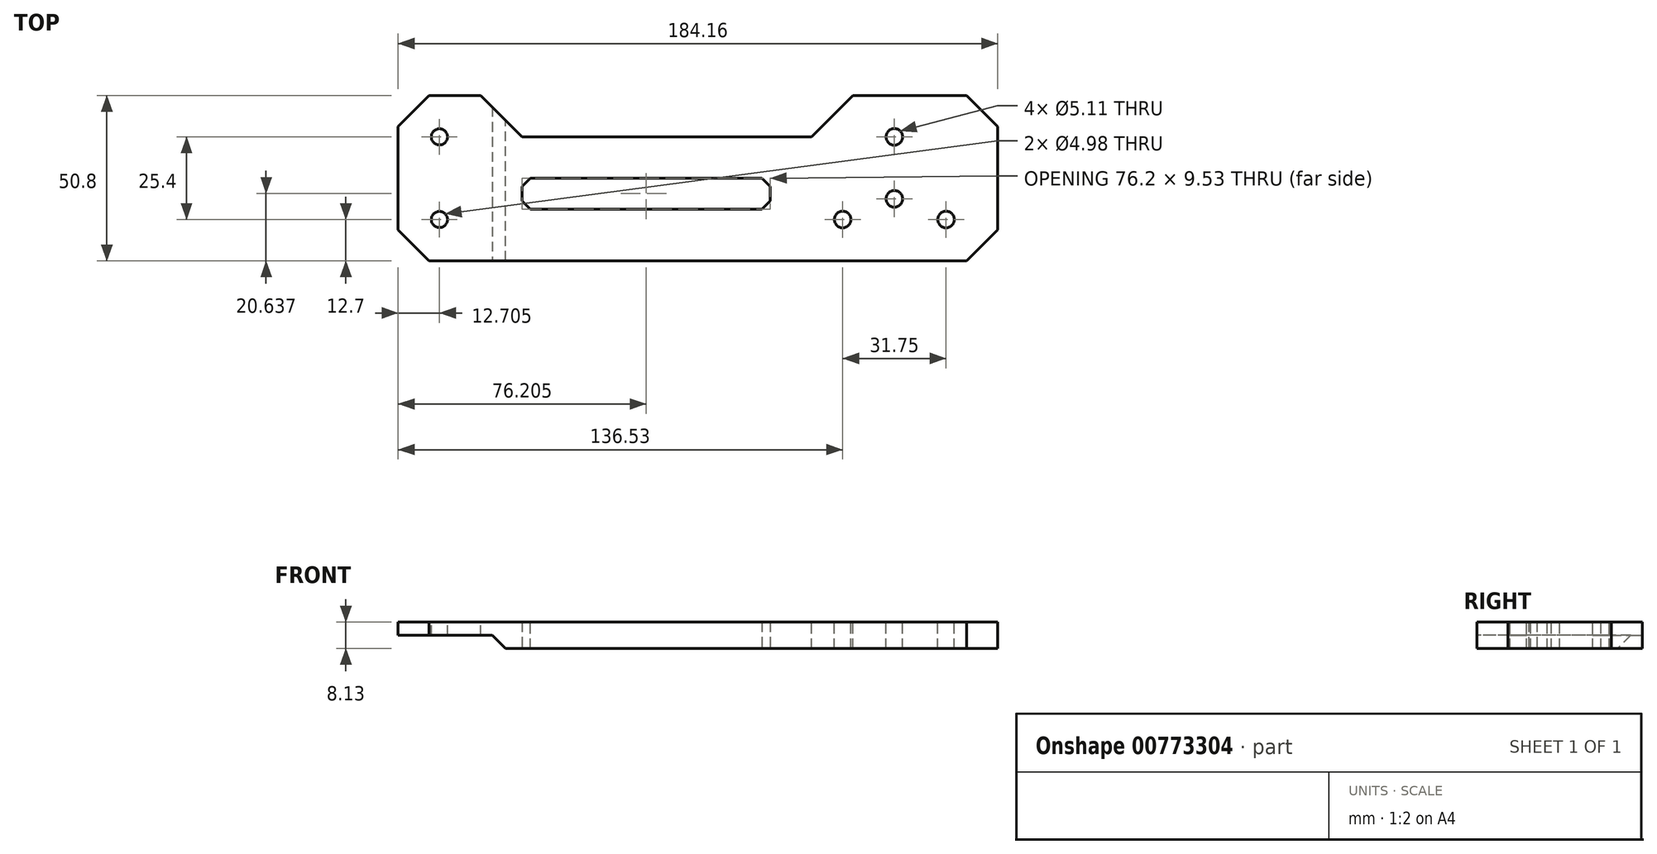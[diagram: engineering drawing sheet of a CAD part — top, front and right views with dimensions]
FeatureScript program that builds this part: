
annotation { "Feature Type Name" : "Feature", "Feature Type Description" : "" }
export const myFeature = defineFeature(function(context is Context, id is Id, definition is map)
    precondition{}
    {
        {
            var Q0;
            Q0=qCreatedBy(makeId("Top.planeOp"),FACE);
            var sketch = newSketch(context, id + "F0", { "sketchPlane" : qUnion([Q0])});
            skLineSegment(sketch, "E0.bottom", {"start": v(-92.08, 25.4) * mm, "end": v(92.08, 25.4) * mm});
            skLineSegment(sketch, "E0.top", {"start": v(-92.08, -25.4) * mm, "end": v(92.08, -25.4) * mm});
            skLineSegment(sketch, "E0.left", {"start": v(-92.08, 25.4) * mm, "end": v(-92.08, -25.4) * mm});
            skLineSegment(sketch, "E0.right", {"start": v(92.08, 25.4) * mm, "end": v(92.08, -25.4) * mm});
            skPoint(sketch, "E0.middle", {"position": v(0, 0) * mm});
            skSolve(sketch);
        }
        {
            var Q0;
            Q0=makeQuery(id+"F0.imprint","IMPRINT",FACE,{"disambiguationData":[TD([[makeQuery(id+"F0.imprint","IMPRINT",EDGE,{"derivedFrom":sQuery(id+"F0.wireOp",EDGE,"E0.bottom")}),-1.0]])]});
            extrude(context, id + "F1", {"entities" : qUnion([Q0]), "depth" : 8.13 * mm, "offsetDistance" : 25.4 * mm});
        }
        {
            var Q0;
            Q0=makeQuery(id+"F1.opExtrude","CAP_FACE",FACE,{"disambiguationData":[OSD([sQuery(id+"F0.wireOp",EDGE,"E0.bottom"),sQuery(id+"F0.wireOp",EDGE,"E0.top"),sQuery(id+"F0.wireOp",EDGE,"E0.left"),sQuery(id+"F0.wireOp",EDGE,"E0.right")])],"isStart":false});
            var sketch = newSketch(context, id + "F2", { "sketchPlane" : qUnion([Q0])});
            skPoint(sketch, "E1", {"position": v(-76.2, -12.7) * mm});
            skPoint(sketch, "E2", {"position": v(-44.45, -12.7) * mm});
            skPoint(sketch, "E3", {"position": v(-60.33, 12.7) * mm});
            skSolve(sketch);
        }
        {
            var Q0;
            Q0=sQuery(id+"F2.wireOp",VERTEX,"E3");
            var Q1;
            Q1=sQuery(id+"F2.wireOp",VERTEX,"E1");
            var Q2;
            Q2=sQuery(id+"F2.wireOp",VERTEX,"E2");
            var Q3;
            Q3=makeQuery(id+"F1.opExtrude","SWEPT_BODY",BODY,{"disambiguationData":[OSD([sQuery(id+"F0.wireOp",EDGE,"E0.bottom"),sQuery(id+"F0.wireOp",EDGE,"E0.top"),sQuery(id+"F0.wireOp",EDGE,"E0.left"),sQuery(id+"F0.wireOp",EDGE,"E0.right")])]});
            hole(context, id + "F3", {"style" : HoleStyle.SIMPLE, "endStyle" : HoleEndStyle.THROUGH, "standardTappedOrClearance" : lookupTablePath({ "standard" : "ANSI", "fit" : "Normal (ASME)", "size" : "#10", "type" : "Clearance" }), "standardBlindInLast" : lookupTablePath({ "fit" : "Free", "standard" : "ANSI", "size" : "#10", "type" : "Clearance" }), "holeDiameter" : 5.1 * mm, "majorDiameter" : 6.35 * mm, "isTappedThrough" : true, "tappedDepth" : 12.7 * mm, "tapClearance" : 3, "locations" : qUnion([Q0, Q1, Q2]), "scope" : qUnion([Q3])});
        }
        {
            var Q0;
            Q0=qCreatedBy(makeId("Right.planeOp"),FACE);
            cPlane(context, id + "F4", {"entities" : qUnion([Q0]), "cplaneType" : CPlaneType.OFFSET, "offset" : 60.32 * mm, "oppositeDirection" : true, "width" : 152.4 * mm, "height" : 152.4 * mm});
        }
        {
            var Q0;
            Q0=makeQuery(id+"F1.opExtrude","CAP_FACE",FACE,{"disambiguationData":[OSD([sQuery(id+"F0.wireOp",EDGE,"E0.bottom"),sQuery(id+"F0.wireOp",EDGE,"E0.top"),sQuery(id+"F0.wireOp",EDGE,"E0.left"),sQuery(id+"F0.wireOp",EDGE,"E0.right")])],"isStart":false});
            var sketch = newSketch(context, id + "F5", { "sketchPlane" : qUnion([Q0])});
            skPoint(sketch, "E4", {"position": v(79.38, 12.7) * mm});
            skPoint(sketch, "E5", {"position": v(79.38, -12.7) * mm});
            skSolve(sketch);
        }
        {
            var Q0;
            Q0=sQuery(id+"F5.wireOp",VERTEX,"E4");
            var Q1;
            Q1=sQuery(id+"F5.wireOp",VERTEX,"E5");
            var Q2;
            Q2=makeQuery(id+"F1.opExtrude","SWEPT_BODY",BODY,{"disambiguationData":[OSD([sQuery(id+"F0.wireOp",EDGE,"E0.bottom"),sQuery(id+"F0.wireOp",EDGE,"E0.top"),sQuery(id+"F0.wireOp",EDGE,"E0.left"),sQuery(id+"F0.wireOp",EDGE,"E0.right")])]});
            hole(context, id + "F6", {"style" : HoleStyle.SIMPLE, "endStyle" : HoleEndStyle.THROUGH, "standardTappedOrClearance" : lookupTablePath({ "standard" : "ANSI", "fit" : "Close", "size" : "#10", "type" : "Clearance" }), "standardBlindInLast" : lookupTablePath({ "fit" : "Close", "standard" : "ANSI", "size" : "#10", "type" : "Clearance" }), "holeDiameter" : 4.98 * mm, "majorDiameter" : 6.35 * mm, "isTappedThrough" : true, "tappedDepth" : 12.7 * mm, "tapClearance" : 3, "locations" : qUnion([Q0, Q1]), "scope" : qUnion([Q2])});
        }
        {
            var Q0;
            Q0=makeQuery(id+"F1.opExtrude","CAP_FACE",FACE,{"disambiguationData":[OSD([sQuery(id+"F0.wireOp",EDGE,"E0.bottom"),sQuery(id+"F0.wireOp",EDGE,"E0.top"),sQuery(id+"F0.wireOp",EDGE,"E0.left"),sQuery(id+"F0.wireOp",EDGE,"E0.right")])],"isStart":false});
            var sketch = newSketch(context, id + "F7", { "sketchPlane" : qUnion([Q0])});
            skLineSegment(sketch, "E6", {"start": v(-47.63, 25.4) * mm, "end": v(-34.92, 12.7) * mm});
            skLineSegment(sketch, "E7", {"start": v(-34.92, 12.7) * mm, "end": v(53.98, 12.7) * mm});
            skLineSegment(sketch, "E8", {"start": v(53.98, 12.7) * mm, "end": v(66.67, 25.4) * mm});
            skLineSegment(sketch, "E9", {"start": v(66.67, 25.4) * mm, "end": v(-47.63, 25.4) * mm});
            skLineSegment(sketch, "E10.bottom", {"start": v(-22.23, 0) * mm, "end": v(53.98, 0) * mm});
            skLineSegment(sketch, "E10.top", {"start": v(-22.23, -9.53) * mm, "end": v(53.98, -9.53) * mm});
            skLineSegment(sketch, "E10.left", {"start": v(-22.23, 0) * mm, "end": v(-22.23, -9.53) * mm});
            skLineSegment(sketch, "E10.right", {"start": v(53.98, 0) * mm, "end": v(53.98, -9.53) * mm});
            skPoint(sketch, "E10.middle", {"position": v(15.88, -4.76) * mm});
            skSolve(sketch);
        }
        {
            var Q0;
            Q0=makeQuery(id+"F7.imprint","IMPRINT",FACE,{"disambiguationData":[TD([[makeQuery(id+"F7.imprint","IMPRINT",EDGE,{"derivedFrom":sQuery(id+"F7.wireOp",EDGE,"E6")}),1.0]])]});
            var Q1;
            Q1=makeQuery(id+"F7.imprint","IMPRINT",FACE,{"disambiguationData":[TD([[makeQuery(id+"F7.imprint","IMPRINT",EDGE,{"derivedFrom":sQuery(id+"F7.wireOp",EDGE,"E10.bottom")}),-1.0]])]});
            extrude(context, id + "F8", {"entities" : qUnion([Q0, Q1]), "operationType" : NewBodyOperationType.REMOVE, "endBound" : BoundingType.THROUGH_ALL, "oppositeDirection" : true, "depth" : 25.4 * mm, "offsetDistance" : 25.4 * mm});
        }
        {
            var Q0;
            Q0=makeQuery(id+"F1.opExtrude","SWEPT_EDGE",EDGE,{"disambiguationData":[OSD([sQuery(id+"F0.wireOp",EDGE,"E0.top"),sQuery(id+"F0.wireOp",EDGE,"E0.left")])]});
            var Q1;
            Q1=makeQuery(id+"F1.opExtrude","SWEPT_EDGE",EDGE,{"disambiguationData":[OSD([sQuery(id+"F0.wireOp",EDGE,"E0.bottom"),sQuery(id+"F0.wireOp",EDGE,"E0.left")])]});
            var Q2;
            Q2=makeQuery(id+"F1.opExtrude","SWEPT_EDGE",EDGE,{"disambiguationData":[OSD([sQuery(id+"F0.wireOp",EDGE,"E0.top"),sQuery(id+"F0.wireOp",EDGE,"E0.right")])]});
            var Q3;
            Q3=makeQuery(id+"F1.opExtrude","SWEPT_EDGE",EDGE,{"disambiguationData":[OSD([sQuery(id+"F0.wireOp",EDGE,"E0.bottom"),sQuery(id+"F0.wireOp",EDGE,"E0.right")])]});
            chamfer(context, id + "F9", {"entities" : qUnion([Q0, Q1, Q2, Q3]), "width" : 9.52 * mm, "tangentPropagation" : true});
        }
        {
            var Q0;
            Q0=makeQuery(id+"F8.boolean.opBoolean","COPY",EDGE,{"derivedFrom":makeQuery(id+"F8.opExtrude","SWEPT_EDGE",EDGE,{"disambiguationData":[OSD([sQuery(id+"F7.wireOp",EDGE,"E10.bottom"),sQuery(id+"F7.wireOp",EDGE,"E10.left")])]})});
            var Q1;
            Q1=makeQuery(id+"F8.boolean.opBoolean","COPY",EDGE,{"derivedFrom":makeQuery(id+"F8.opExtrude","SWEPT_EDGE",EDGE,{"disambiguationData":[OSD([sQuery(id+"F7.wireOp",EDGE,"E10.top"),sQuery(id+"F7.wireOp",EDGE,"E10.left")])]})});
            var Q2;
            Q2=makeQuery(id+"F8.boolean.opBoolean","COPY",EDGE,{"derivedFrom":makeQuery(id+"F8.opExtrude","SWEPT_EDGE",EDGE,{"disambiguationData":[OSD([sQuery(id+"F7.wireOp",EDGE,"E10.bottom"),sQuery(id+"F7.wireOp",EDGE,"E10.right")])]})});
            var Q3;
            Q3=makeQuery(id+"F8.boolean.opBoolean","COPY",EDGE,{"derivedFrom":makeQuery(id+"F8.opExtrude","SWEPT_EDGE",EDGE,{"disambiguationData":[OSD([sQuery(id+"F7.wireOp",EDGE,"E10.top"),sQuery(id+"F7.wireOp",EDGE,"E10.right")])]})});
            chamfer(context, id + "F10", {"entities" : qUnion([Q0, Q1, Q2, Q3]), "width" : 2.54 * mm, "tangentPropagation" : true});
        }
        {
            var Q0;
            Q0=makeQuery(id+"F1.opExtrude","CAP_FACE",FACE,{"disambiguationData":[OSD([sQuery(id+"F0.wireOp",EDGE,"E0.bottom"),sQuery(id+"F0.wireOp",EDGE,"E0.top"),sQuery(id+"F0.wireOp",EDGE,"E0.left"),sQuery(id+"F0.wireOp",EDGE,"E0.right")])],"isStart":false});
            var sketch = newSketch(context, id + "F11", { "sketchPlane" : qUnion([Q0])});
            skLineSegment(sketch, "E11", {"start": v(66.67, 25.4) * mm, "end": v(66.67, -25.4) * mm});
            skLineSegment(sketch, "E12", {"start": v(66.67, -25.4) * mm, "end": v(82.55, -25.4) * mm});
            skLineSegment(sketch, "E13", {"start": v(82.55, -25.4) * mm, "end": v(92.08, -15.88) * mm});
            skLineSegment(sketch, "E14", {"start": v(92.08, -15.88) * mm, "end": v(92.08, 15.88) * mm});
            skLineSegment(sketch, "E15", {"start": v(92.08, 15.88) * mm, "end": v(82.55, 25.4) * mm});
            skLineSegment(sketch, "E16", {"start": v(82.55, 25.4) * mm, "end": v(66.67, 25.4) * mm});
            skSolve(sketch);
        }
        {
            var Q0;
            Q0=makeQuery(id+"F1.opExtrude","SWEPT_FACE",FACE,{"disambiguationData":[OSD([sQuery(id+"F0.wireOp",EDGE,"E0.right")])]});
            cPlane(context, id + "F12", {"entities" : qUnion([Q0]), "cplaneType" : CPlaneType.OFFSET, "offset" : 0 * mm, "width" : 152.4 * mm, "height" : 152.4 * mm});
        }
        {
            var Q0;
            Q0=makeQuery(id+"F1.opExtrude","SWEPT_BODY",BODY,{"disambiguationData":[OSD([sQuery(id+"F0.wireOp",EDGE,"E0.bottom"),sQuery(id+"F0.wireOp",EDGE,"E0.top"),sQuery(id+"F0.wireOp",EDGE,"E0.left"),sQuery(id+"F0.wireOp",EDGE,"E0.right")])]});
            var Q1;
            Q1=qCreatedBy(id+"F12.planeOp",FACE);
            mirror(context, id + "F13", {"entities" : qUnion([Q0]), "mirrorPlane" : qUnion([Q1])});
        }
        {
            var Q0;
            Q0=makeQuery(id+"F13.opPattern","COPY",FACE,{"derivedFrom":makeQuery(id+"F1.opExtrude","CAP_FACE",FACE,{"disambiguationData":[OSD([sQuery(id+"F0.wireOp",EDGE,"E0.bottom"),sQuery(id+"F0.wireOp",EDGE,"E0.top"),sQuery(id+"F0.wireOp",EDGE,"E0.left"),sQuery(id+"F0.wireOp",EDGE,"E0.right")])],"isStart":false}),"instanceName":"1"});
            var sketch = newSketch(context, id + "F14", { "sketchPlane" : qUnion([Q0])});
            skLineSegment(sketch, "E17.bottom", {"start": v(92.08, -25.4) * mm, "end": v(-100.56, -25.4) * mm});
            skLineSegment(sketch, "E17.top", {"start": v(92.08, 34.01) * mm, "end": v(-100.56, 34.01) * mm});
            skLineSegment(sketch, "E17.left", {"start": v(92.08, -25.4) * mm, "end": v(92.08, 34.01) * mm});
            skLineSegment(sketch, "E17.right", {"start": v(-100.56, -25.4) * mm, "end": v(-100.56, 34.01) * mm});
            skSolve(sketch);
        }
        {
            var Q0;
            {var subQ7=sQuery(id+"F14.wireOp",EDGE,"E17.bottom");Q0=makeQuery(id+"F14.imprint","IMPRINT",FACE,{"disambiguationData":[TD([[makeQuery(id+"F14.imprint","IMPRINT",EDGE,{"derivedFrom":subQ7}),-1.0]])]});}
            extrude(context, id + "F15", {"entities" : qUnion([Q0]), "operationType" : NewBodyOperationType.REMOVE, "oppositeDirection" : true, "depth" : 25.4 * mm, "offsetDistance" : 25.4 * mm});
        }
        {
            var Q0;
            Q0=makeQuery(id+"F13.opPattern","COPY",FACE,{"derivedFrom":makeQuery(id+"F1.opExtrude","CAP_FACE",FACE,{"disambiguationData":[OSD([sQuery(id+"F0.wireOp",EDGE,"E0.bottom"),sQuery(id+"F0.wireOp",EDGE,"E0.top"),sQuery(id+"F0.wireOp",EDGE,"E0.left"),sQuery(id+"F0.wireOp",EDGE,"E0.right")])],"isStart":false}),"instanceName":"1"});
            var sketch = newSketch(context, id + "F16", { "sketchPlane" : qUnion([Q0])});
            skPoint(sketch, "E18", {"position": v(244.47, -6.35) * mm});
            skSolve(sketch);
        }
        {
            var Q0;
            Q0=sQuery(id+"F16.wireOp",VERTEX,"E18");
            var Q1;
            Q1=makeQuery(id+"F13.opPattern","COPY",BODY,{"derivedFrom":makeQuery(id+"F1.opExtrude","SWEPT_BODY",BODY,{"disambiguationData":[OSD([sQuery(id+"F0.wireOp",EDGE,"E0.bottom"),sQuery(id+"F0.wireOp",EDGE,"E0.top"),sQuery(id+"F0.wireOp",EDGE,"E0.left"),sQuery(id+"F0.wireOp",EDGE,"E0.right")])]}),"instanceName":"1"});
            hole(context, id + "F17", {"style" : HoleStyle.SIMPLE, "endStyle" : HoleEndStyle.THROUGH, "standardTappedOrClearance" : lookupTablePath({ "standard" : "ANSI", "fit" : "Normal (ASME)", "size" : "#10", "type" : "Clearance" }), "standardBlindInLast" : lookupTablePath({ "fit" : "Free", "standard" : "ANSI", "size" : "#10", "type" : "Clearance" }), "holeDiameter" : 5.1 * mm, "majorDiameter" : 6.35 * mm, "isTappedThrough" : true, "tappedDepth" : 12.7 * mm, "tapClearance" : 3, "locations" : qUnion([Q0]), "scope" : qUnion([Q1])});
        }
        {
            var Q0;
            Q0=makeQuery(id+"F13.opPattern","COPY",FACE,{"derivedFrom":makeQuery(id+"F1.opExtrude","CAP_FACE",FACE,{"disambiguationData":[OSD([sQuery(id+"F0.wireOp",EDGE,"E0.bottom"),sQuery(id+"F0.wireOp",EDGE,"E0.top"),sQuery(id+"F0.wireOp",EDGE,"E0.left"),sQuery(id+"F0.wireOp",EDGE,"E0.right")])],"isStart":true}),"instanceName":"1"});
            var sketch = newSketch(context, id + "F18", { "sketchPlane" : qUnion([Q0])});
            skLineSegment(sketch, "E19", {"start": v(117.48, 25.4) * mm, "end": v(101.6, 25.4) * mm});
            skLineSegment(sketch, "E20", {"start": v(101.6, 25.4) * mm, "end": v(92.08, 15.88) * mm});
            skLineSegment(sketch, "E21", {"start": v(92.08, -15.88) * mm, "end": v(92.08, 15.88) * mm});
            skLineSegment(sketch, "E22", {"start": v(92.07, -15.88) * mm, "end": v(101.6, -25.4) * mm});
            skLineSegment(sketch, "E23", {"start": v(101.6, -25.4) * mm, "end": v(117.48, -25.4) * mm});
            skLineSegment(sketch, "E24", {"start": v(117.48, 25.4) * mm, "end": v(125.1, 25.4) * mm});
            skLineSegment(sketch, "E25", {"start": v(125.1, 25.4) * mm, "end": v(125.1, -17.78) * mm});
            skLineSegment(sketch, "E26", {"start": v(125.1, -17.78) * mm, "end": v(117.48, -25.4) * mm});
            skSolve(sketch);
        }
        {
            var Q0;
            Q0=makeQuery(id+"F18.imprint","IMPRINT",FACE,{"disambiguationData":[TD([[makeQuery(id+"F18.imprint","IMPRINT",EDGE,{"derivedFrom":sQuery(id+"F18.wireOp",EDGE,"E19")}),1.0]])]});
            extrude(context, id + "F19", {"entities" : qUnion([Q0]), "operationType" : NewBodyOperationType.REMOVE, "oppositeDirection" : true, "depth" : 4.06 * mm, "offsetDistance" : 25.4 * mm});
        }
        {
            var Q0;
            Q0=makeQuery(id+"F19.boolean.opBoolean","COPY",EDGE,{"derivedFrom":makeQuery(id+"F19.opExtrude","CAP_EDGE",EDGE,{"disambiguationData":[OSD([sQuery(id+"F18.wireOp",EDGE,"lfiL7zHA-pyFF-QQtH-J0Cy-HWtlnDw31Qwt")])],"isStart":false})});
            var Q1;
            Q1=makeQuery(id+"F19.boolean.opBoolean","COPY",EDGE,{"derivedFrom":makeQuery(id+"F19.opExtrude","CAP_EDGE",EDGE,{"disambiguationData":[OSD([sQuery(id+"F18.wireOp",EDGE,"E25")])],"isStart":false})});
            chamfer(context, id + "F20", {"entities" : qUnion([Q0, Q1]), "width" : 4.06 * mm, "tangentPropagation" : true});
        }
    });
